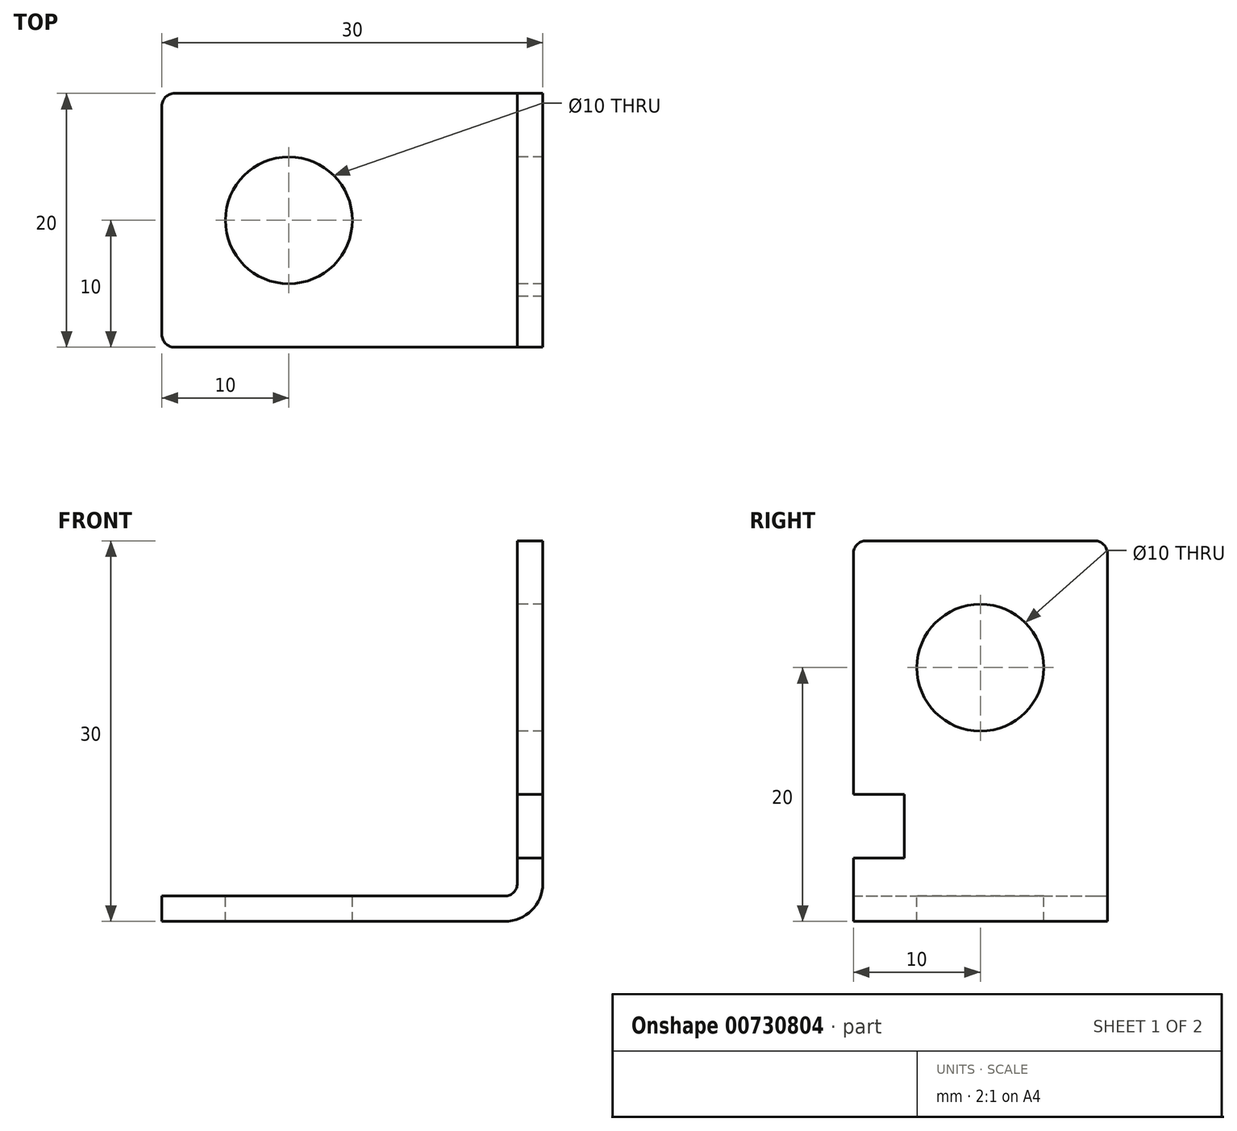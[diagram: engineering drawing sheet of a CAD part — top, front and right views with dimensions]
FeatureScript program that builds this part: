
annotation { "Feature Type Name" : "Feature", "Feature Type Description" : "" }
export const myFeature = defineFeature(function(context is Context, id is Id, definition is map)
    precondition{}
    {
        {
            var Q0;
            Q0=qCreatedBy(makeId("Front.planeOp"),FACE);
            var sketch = newSketch(context, id + "F0", { "sketchPlane" : qUnion([Q0])});
            skLineSegment(sketch, "E0", {"start": v(0, 0) * mm, "end": v(27, 0) * mm});
            skLineSegment(sketch, "E1", {"start": v(30, 3) * mm, "end": v(30, 30) * mm});
            skLineSegment(sketch, "E2", {"start": v(30, 30) * mm, "end": v(28, 30) * mm});
            skLineSegment(sketch, "E3", {"start": v(28, 30) * mm, "end": v(28, 3) * mm});
            skLineSegment(sketch, "E4", {"start": v(27, 2) * mm, "end": v(0, 2) * mm});
            skLineSegment(sketch, "E5", {"start": v(0, 2) * mm, "end": v(0, 0) * mm});
            skPoint(sketch, "E6.visualSharp", {"position": v(30, 0) * mm});
            skArc(sketch, "E6.filletArc", {"start": v(27, 0) * mm, "mid": v(29.12, 0.88) * mm, "end": v(30, 3) * mm});
            skPoint(sketch, "E7.visualSharp", {"position": v(28, 2) * mm});
            skArc(sketch, "E7.filletArc", {"start": v(27, 2) * mm, "mid": v(27.7, 2.3) * mm, "end": v(28, 3) * mm});
            skSolve(sketch);
        }
        {
            var Q0;
            Q0=makeQuery(id+"F0.imprint","IMPRINT",FACE,{"disambiguationData":[TD([[makeQuery(id+"F0.imprint","IMPRINT",EDGE,{"derivedFrom":sQuery(id+"F0.wireOp",EDGE,"E0")}),1.0]])]});
            extrude(context, id + "F1", {"entities" : qUnion([Q0]), "depth" : 20 * mm, "offsetDistance" : 25 * mm});
        }
        {
            var Q0;
            Q0=makeQuery(id+"F1.opExtrude","CAP_EDGE",EDGE,{"disambiguationData":[OSD([sQuery(id+"F0.wireOp",EDGE,"E2")])],"isStart":true});
            var Q1;
            Q1=makeQuery(id+"F1.opExtrude","CAP_EDGE",EDGE,{"disambiguationData":[OSD([sQuery(id+"F0.wireOp",EDGE,"E2")])],"isStart":false});
            var Q2;
            Q2=makeQuery(id+"F1.opExtrude","CAP_EDGE",EDGE,{"disambiguationData":[OSD([sQuery(id+"F0.wireOp",EDGE,"E5")])],"isStart":false});
            var Q3;
            Q3=makeQuery(id+"F1.opExtrude","CAP_EDGE",EDGE,{"disambiguationData":[OSD([sQuery(id+"F0.wireOp",EDGE,"E5")])],"isStart":true});
            fillet(context, id + "F2", {"entities" : qUnion([Q0, Q1, Q2, Q3]), "radius" : 1 * mm, "tangentPropagation" : true, "allowEdgeOverflow" : false});
        }
        {
            var Q0;
            Q0=makeQuery(id+"F1.opExtrude","SWEPT_FACE",FACE,{"disambiguationData":[OSD([sQuery(id+"F0.wireOp",EDGE,"E3")])]});
            var sketch = newSketch(context, id + "F3", { "sketchPlane" : qUnion([Q0])});
            skCircle(sketch, "E8", {"center": v(10, 20) * mm, "radius": 5 * mm});
            skPoint(sketch, "E8.centerSnap0", {"position": v(10, 30) * mm});
            skLineSegment(sketch, "E9.bottom", {"start": v(20, 10) * mm, "end": v(16, 10) * mm});
            skLineSegment(sketch, "E9.top", {"start": v(20, 5) * mm, "end": v(16, 5) * mm});
            skLineSegment(sketch, "E9.left", {"start": v(20, 10) * mm, "end": v(20, 5) * mm});
            skLineSegment(sketch, "E9.right", {"start": v(16, 10) * mm, "end": v(16, 5) * mm});
            skSolve(sketch);
        }
        {
            var Q0;
            Q0=makeQuery(id+"F3.imprint","IMPRINT",FACE,{"disambiguationData":[TD([[makeQuery(id+"F3.imprint","IMPRINT",EDGE,{"derivedFrom":sQuery(id+"F3.wireOp",EDGE,"E8")}),1.0]])]});
            var Q1;
            Q1=makeQuery(id+"F3.imprint","IMPRINT",FACE,{"disambiguationData":[TD([[makeQuery(id+"F3.imprint","IMPRINT",EDGE,{"derivedFrom":sQuery(id+"F3.wireOp",EDGE,"E9.bottom")}),1.0]])]});
            extrude(context, id + "F4", {"entities" : qUnion([Q0, Q1]), "operationType" : NewBodyOperationType.REMOVE, "endBound" : BoundingType.THROUGH_ALL, "oppositeDirection" : true, "depth" : 25 * mm, "offsetDistance" : 25 * mm});
        }
        {
            var Q0;
            Q0=makeQuery(id+"F1.opExtrude","SWEPT_FACE",FACE,{"disambiguationData":[OSD([sQuery(id+"F0.wireOp",EDGE,"E4")])]});
            var sketch = newSketch(context, id + "F5", { "sketchPlane" : qUnion([Q0])});
            skCircle(sketch, "E10", {"center": v(10, -10) * mm, "radius": 5 * mm});
            skPoint(sketch, "E10.centerSnap0", {"position": v(0, -10) * mm});
            skSolve(sketch);
        }
        {
            var Q0;
            Q0=makeQuery(id+"F5.imprint","IMPRINT",FACE,{"disambiguationData":[TD([[makeQuery(id+"F5.imprint","IMPRINT",EDGE,{"derivedFrom":sQuery(id+"F5.wireOp",EDGE,"E10")}),1.0]])]});
            extrude(context, id + "F6", {"entities" : qUnion([Q0]), "operationType" : NewBodyOperationType.REMOVE, "endBound" : BoundingType.THROUGH_ALL, "oppositeDirection" : true, "depth" : 25 * mm, "offsetDistance" : 25 * mm});
        }
    });
